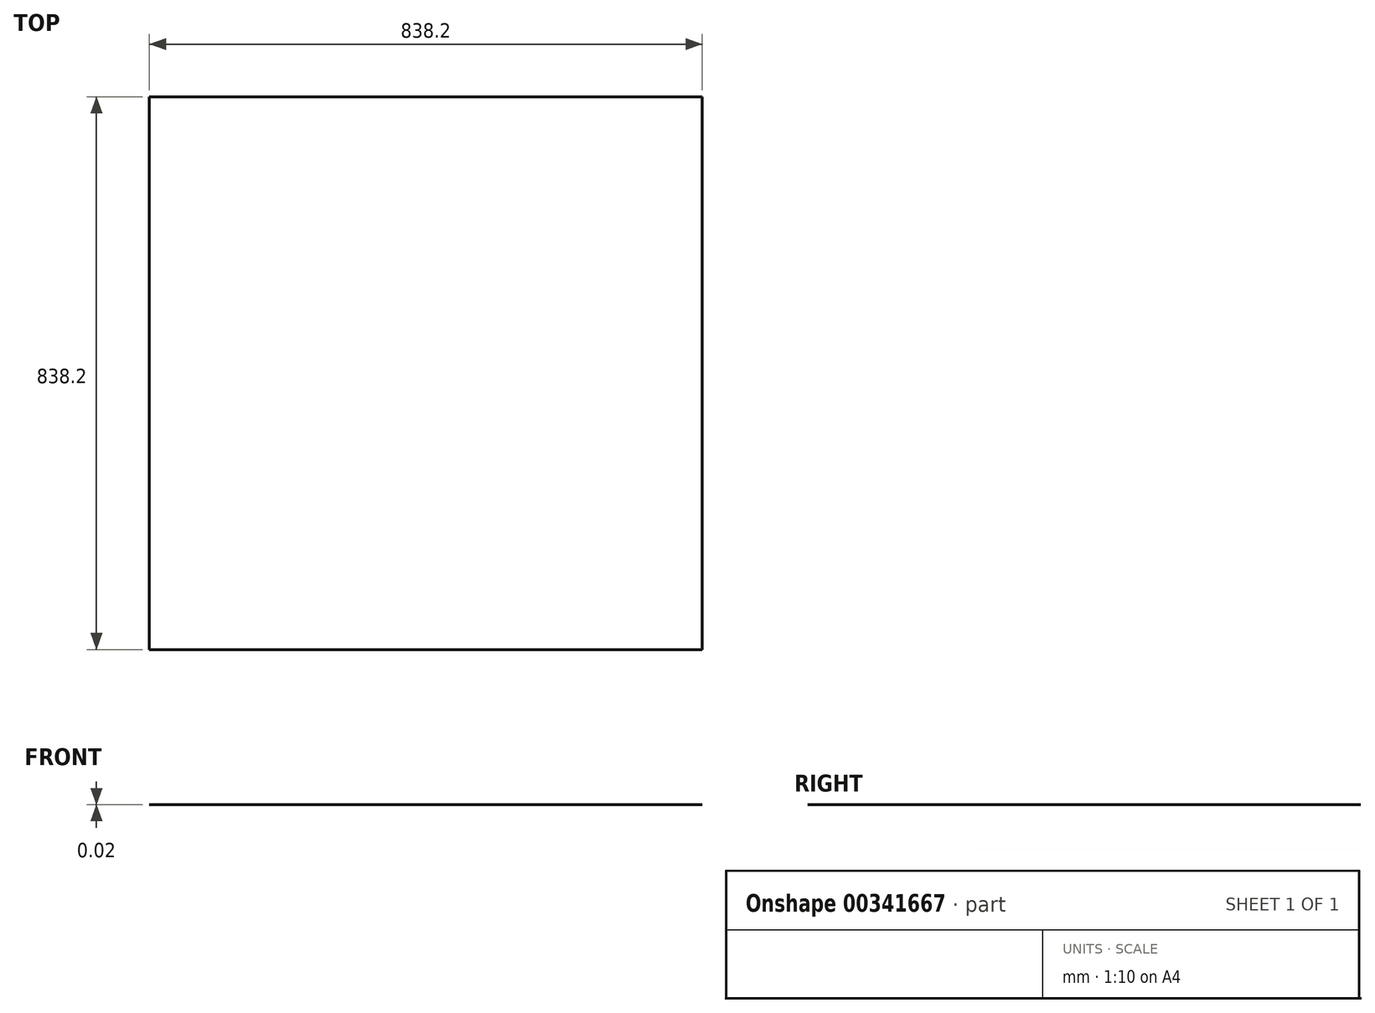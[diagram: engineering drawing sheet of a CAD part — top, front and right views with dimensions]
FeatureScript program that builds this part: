
annotation { "Feature Type Name" : "Feature", "Feature Type Description" : "" }
export const myFeature = defineFeature(function(context is Context, id is Id, definition is map)
    precondition{}
    {
        {
            var Q0;
            Q0=qCreatedBy(makeId("Top.planeOp"),FACE);
            var sketch = newSketch(context, id + "F0", { "sketchPlane" : qUnion([Q0])});
            skLineSegment(sketch, "E0.bottom", {"start": v(-430.32, -329.66) * mm, "end": v(407.88, -329.66) * mm});
            skLineSegment(sketch, "E0.top", {"start": v(-430.32, 508.54) * mm, "end": v(407.88, 508.54) * mm});
            skLineSegment(sketch, "E0.left", {"start": v(-430.32, -329.66) * mm, "end": v(-430.32, 508.54) * mm});
            skLineSegment(sketch, "E0.right", {"start": v(407.88, -329.66) * mm, "end": v(407.88, 508.54) * mm});
            skSolve(sketch);
        }
        {
            var Q0;
            Q0=makeQuery(id+"F0.imprint","IMPRINT",FACE,{"disambiguationData":[TD([[makeQuery(id+"F0.imprint","IMPRINT",EDGE,{"derivedFrom":sQuery(id+"F0.wireOp",EDGE,"E0.bottom")}),1.0]])]});
            extrude(context, id + "F1", {"entities" : qUnion([Q0]), "depth" : 1 / 50.8 * mm});
        }
    });
